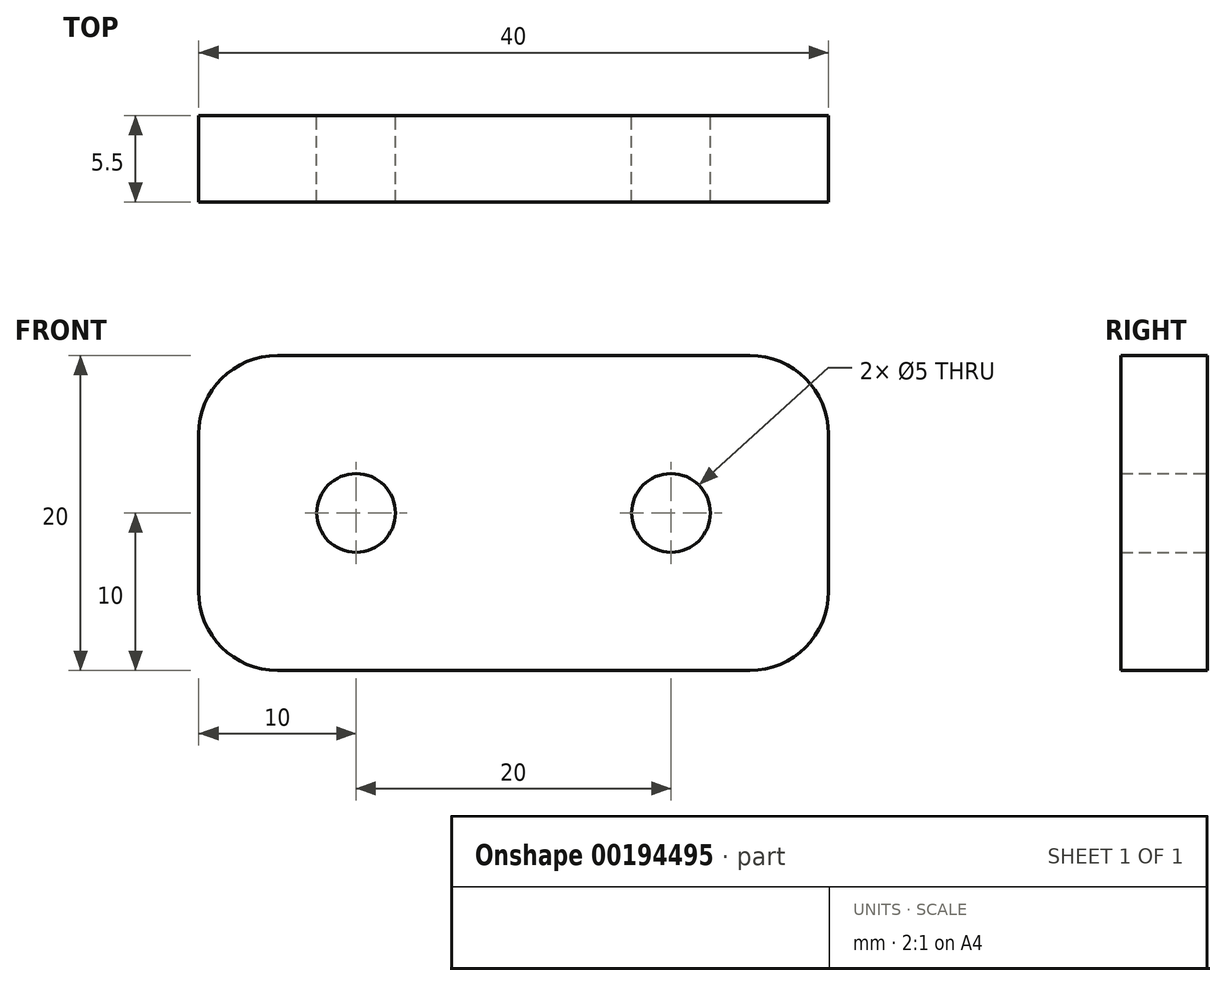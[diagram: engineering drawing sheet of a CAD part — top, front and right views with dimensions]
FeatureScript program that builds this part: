
annotation { "Feature Type Name" : "Feature", "Feature Type Description" : "" }
export const myFeature = defineFeature(function(context is Context, id is Id, definition is map)
    precondition{}
    {
        {
            var Q0;
            Q0=qCreatedBy(makeId("Front.planeOp"),FACE);
            var sketch = newSketch(context, id + "F0", { "sketchPlane" : qUnion([Q0])});
            skLineSegment(sketch, "E0.bottom", {"start": v(15, 10) * mm, "end": v(-15, 10) * mm});
            skLineSegment(sketch, "E0.top", {"start": v(15, -10) * mm, "end": v(-15, -10) * mm});
            skLineSegment(sketch, "E0.left", {"start": v(20, 5) * mm, "end": v(20, -5) * mm});
            skLineSegment(sketch, "E0.right", {"start": v(-20, 5) * mm, "end": v(-20, -5) * mm});
            skPoint(sketch, "E0.middle", {"position": v(0, 0) * mm});
            skPoint(sketch, "E1.visualSharp", {"position": v(-20, 10) * mm});
            skArc(sketch, "E1.filletArc", {"start": v(-15, 10) * mm, "mid": v(-18.54, 8.54) * mm, "end": v(-20, 5) * mm});
            skPoint(sketch, "E2.visualSharp", {"position": v(20, 10) * mm});
            skArc(sketch, "E2.filletArc", {"start": v(20, 5) * mm, "mid": v(18.54, 8.54) * mm, "end": v(15, 10) * mm});
            skPoint(sketch, "E3.visualSharp", {"position": v(20, -10) * mm});
            skArc(sketch, "E3.filletArc", {"start": v(15, -10) * mm, "mid": v(18.54, -8.54) * mm, "end": v(20, -5) * mm});
            skPoint(sketch, "E4.visualSharp", {"position": v(-20, -10) * mm});
            skArc(sketch, "E4.filletArc", {"start": v(-20, -5) * mm, "mid": v(-18.54, -8.54) * mm, "end": v(-15, -10) * mm});
            skPoint(sketch, "E5", {"position": v(-10, 0) * mm});
            skPoint(sketch, "E6", {"position": v(10, 0) * mm});
            skCircle(sketch, "E7", {"center": v(-10, 0) * mm, "radius": 2.5 * mm});
            skCircle(sketch, "E8", {"center": v(10, 0) * mm, "radius": 2.5 * mm});
            skSolve(sketch);
        }
        {
            var Q0;
            Q0=makeQuery(id+"F0.imprint","IMPRINT",FACE,{"disambiguationData":[TD([[makeQuery(id+"F0.imprint","IMPRINT",EDGE,{"derivedFrom":sQuery(id+"F0.wireOp",EDGE,"E0.bottom")}),1.0]])]});
            extrude(context, id + "F1", {"entities" : qUnion([Q0]), "depth" : 5.5 * mm});
        }
    });
